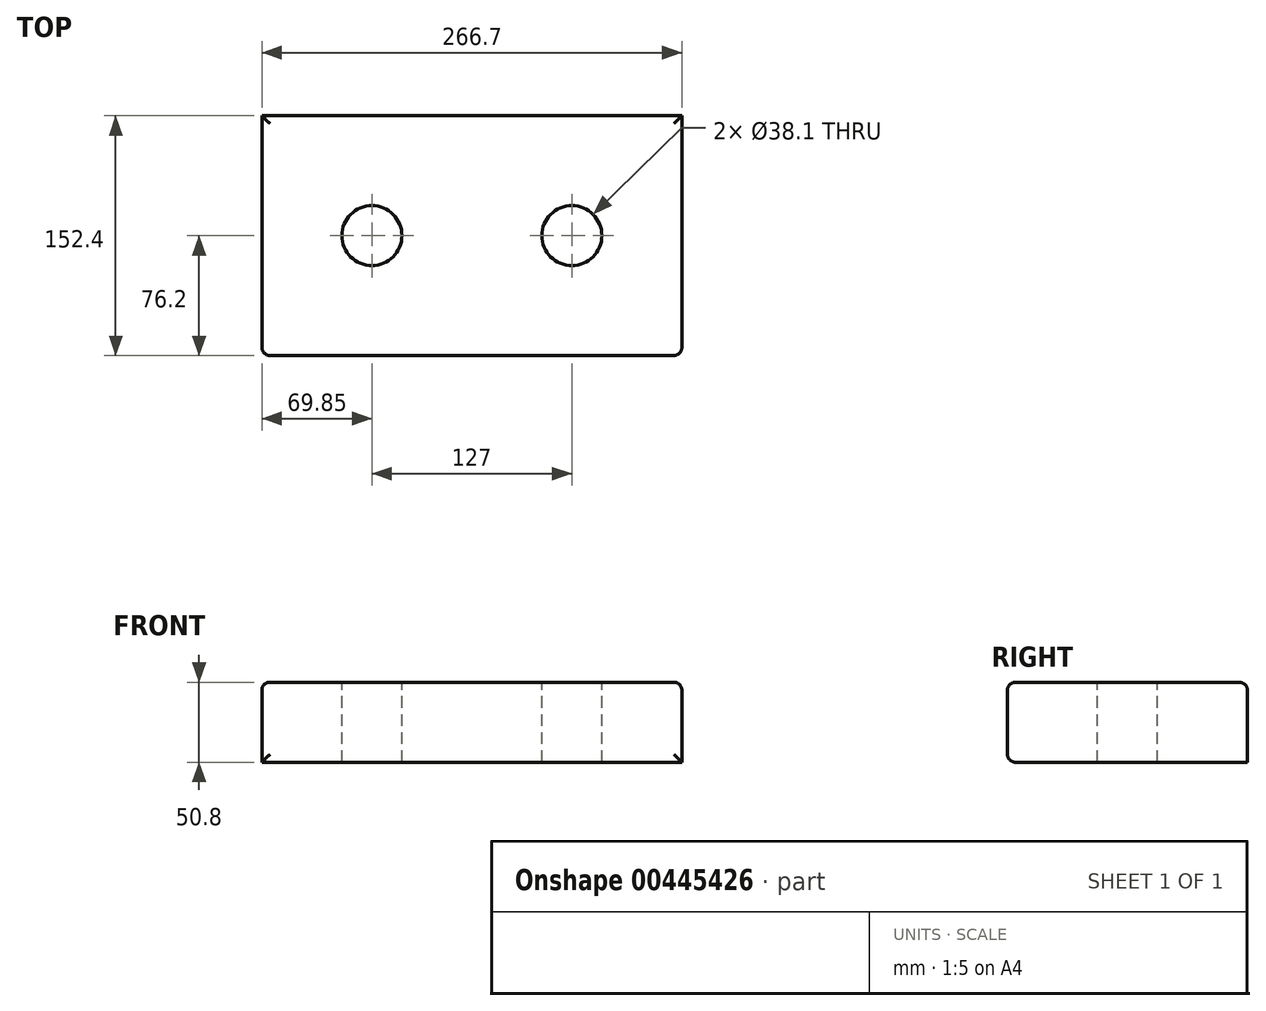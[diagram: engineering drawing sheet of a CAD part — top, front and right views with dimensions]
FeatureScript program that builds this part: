
annotation { "Feature Type Name" : "Feature", "Feature Type Description" : "" }
export const myFeature = defineFeature(function(context is Context, id is Id, definition is map)
    precondition{}
    {
        {
            var Q0;
            Q0=qCreatedBy(makeId("Top.planeOp"),FACE);
            var sketch = newSketch(context, id + "F0", { "sketchPlane" : qUnion([Q0])});
            skLineSegment(sketch, "E0.bottom", {"start": v(133.35, 76.2) * mm, "end": v(-133.35, 76.2) * mm});
            skLineSegment(sketch, "E0.top", {"start": v(133.35, -76.2) * mm, "end": v(-133.35, -76.2) * mm});
            skLineSegment(sketch, "E0.left", {"start": v(133.35, 76.2) * mm, "end": v(133.35, -76.2) * mm});
            skLineSegment(sketch, "E0.right", {"start": v(-133.35, 76.2) * mm, "end": v(-133.35, -76.2) * mm});
            skPoint(sketch, "E0.middle", {"position": v(0, 0) * mm});
            skCircle(sketch, "E1", {"center": v(0, 0) * mm, "radius": 19.05 * mm});
            skCircle(sketch, "E2", {"center": v(-63.5, 0) * mm, "radius": 19.05 * mm});
            skCircle(sketch, "E3", {"center": v(63.5, 0) * mm, "radius": 19.05 * mm});
            skSolve(sketch);
        }
        {
            var Q0;
            Q0 = qSketchRegion(id + "F0", true);
            var Q1;
            {var subQ0=sQuery(id+"F0.wireOp",EDGE,"E1");var subQ1=makeQuery(id+"F0.imprint","INTERSECT",VERTEX,{"derivedFrom":[subQ0,sQuery(id+"F0.wireOp",EDGE,"E2")]});Q1=makeQuery(id+"F0.imprint","IMPRINT",FACE,{"disambiguationData":[TD([[makeQuery(id+"F0.imprint","IMPRINT",EDGE,{"disambiguationData":[TD([[subQ1,1.0]])],"derivedFrom":subQ0}),1.0]])]});}
            extrude(context, id + "F1", {"entities" : qUnion([Q0, Q1]), "oppositeDirection" : true, "depth" : 50.8 * mm});
        }
        {
            var Q0;
            Q0=makeQuery(id+"F1.opExtrude","CAP_EDGE",EDGE,{"disambiguationData":[OSD([sQuery(id+"F0.wireOp",EDGE,"E0.right")])],"isStart":true});
            var Q1;
            Q1=makeQuery(id+"F1.opExtrude","CAP_EDGE",EDGE,{"disambiguationData":[OSD([sQuery(id+"F0.wireOp",EDGE,"E0.bottom")])],"isStart":true});
            var Q2;
            Q2=makeQuery(id+"F1.opExtrude","CAP_EDGE",EDGE,{"disambiguationData":[OSD([sQuery(id+"F0.wireOp",EDGE,"E0.left")])],"isStart":true});
            var Q3;
            Q3=makeQuery(id+"F1.opExtrude","SWEPT_FACE",FACE,{"disambiguationData":[OSD([sQuery(id+"F0.wireOp",EDGE,"E0.top")])]});
            fillet(context, id + "F2", {"entities" : qUnion([Q0, Q1, Q2, Q3]), "radius" : 5.08 * mm, "tangentPropagation" : true, "allowEdgeOverflow" : false});
        }
    });
